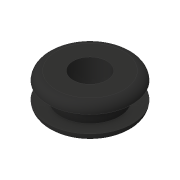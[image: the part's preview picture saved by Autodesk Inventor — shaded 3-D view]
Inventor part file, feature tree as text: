
AUTODESK INVENTOR PART (.ipt)
format: ipt  version: 2019.4 (Build 234330000, 330)  size: 125,440 bytes
history: native  units: in
note: dims shown in document units (in); Inventor stores cm internally (conversion verified against a paired STEP export)
features: revolve x1
ambient origin geometry x8: Origin, YZ Plane, XZ Plane, XY Plane, X Axis, Y Axis, Z Axis, Center Point
bodies: Solid1 (feature_tree)
feature tree (1):
  revolve  "Revolve1"  [1 undecoded]
note: 1 required parameter value undecoded (feature->parameter linkage not recoverable at this tier; creation-order binding heuristic only, values carry confidence <= 0.55)
